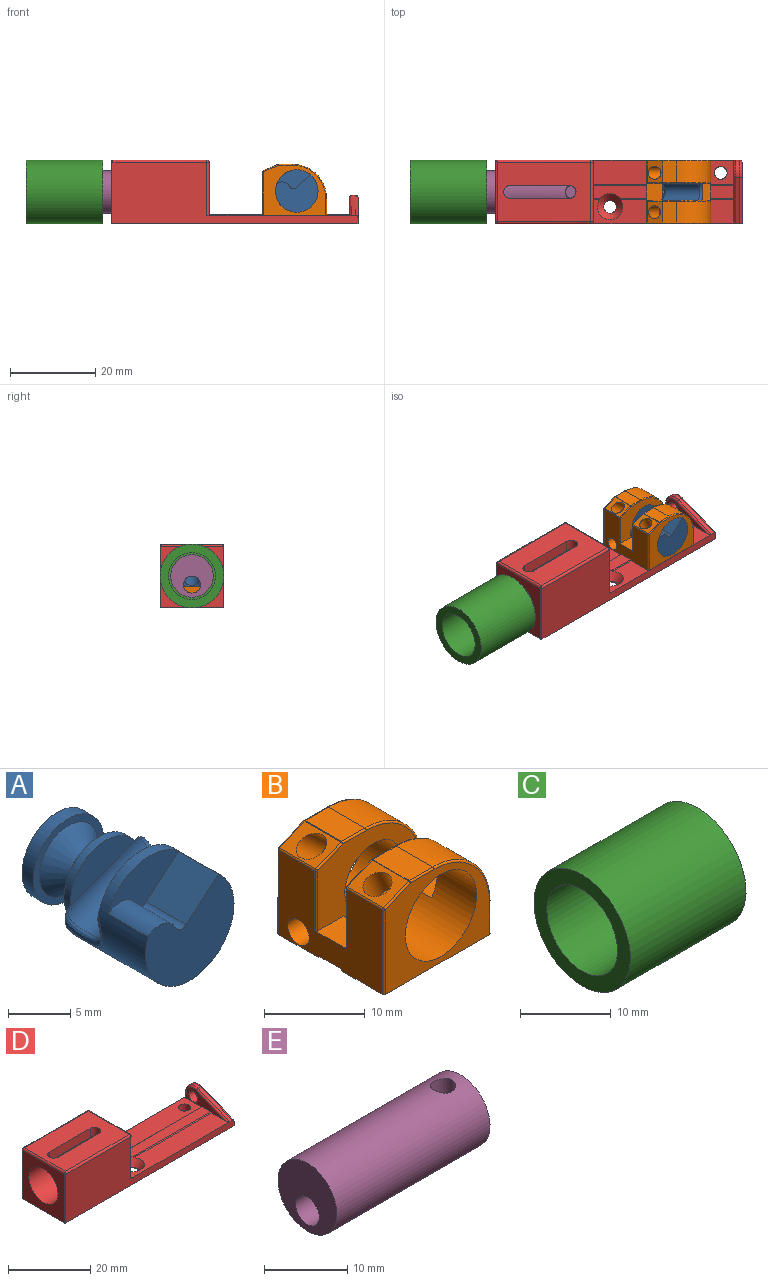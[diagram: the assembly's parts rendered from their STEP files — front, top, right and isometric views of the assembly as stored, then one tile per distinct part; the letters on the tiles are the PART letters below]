
ASSEMBLY  parts=5 mates=5
PART A: 19 faces, bbox 10.2x15.2x10.2 mm
  f0: plane 9.77x7.65mm, normal (0,1,0), area 15.6mm2, adj f1,f3,f15,f17,f18
  f1: cylinder r=5mm len=10mm, axis (0,-1,0), area 180.1mm2, adj f0,f2,f10,f12,f13,f16,f17,f18
  f2: plane 10x8.83mm, normal (0,-1,0), area 59.1mm2, adj f1,f10,f11,f12
  f3: cylinder r=4mm len=8mm, axis (0,1,0), area 18.8mm2, adj f0,f5,f14
  f4: cone r=3.31mm half-angle=45deg, axis (0,-1,0), area 37.8mm2, adj f5,f7
  f5: plane 8x8mm, normal (0,1,0), area 15.9mm2, adj f3,f4
  f6: plane 8x8mm, normal (0,-1,0), area 15.9mm2, adj f7,f9
  f7: cone r=1.56mm half-angle=45deg, axis (0,1,0), area 37.8mm2, adj f4,f6
  f8: plane 8x8mm, normal (0,1,0), area 50.3mm2, adj f9
  f9: cylinder r=4mm len=8mm, axis (0,1,0), area 31.4mm2, adj f6,f8
  f10: cylinder r=2mm len=4.5mm, axis (0,-1,0), area 16.7mm2, adj f1,f2,f11,f13
  f11: cylinder r=0.75mm len=4.5mm, axis (0,-1,0), area 6.3mm2, adj f2,f10,f12,f13
  f12: plane 4.5x3.63mm, normal (-0.65,0,0.76), area 21.6mm2, adj f1,f2,f11,f13
  f13: plane 7.93x4.49mm, normal (0,-1,0), area 19.4mm2, adj f1,f10,f11,f12
  f14: plane 7.26x4.44mm, normal (0,-1,0), area 17.2mm2, adj f3,f15
  f15: cylinder r=2mm len=8.91mm, axis (-0.93,0,-0.36), area 55.1mm2, adj f0,f14,f16,f17,f18
  f16: plane 8.81x5.78mm, normal (0,1,0), area 28.6mm2, adj f1,f15,f17,f18
  f17: bspline ~5x4.19mm, area 6.2mm2, adj f0,f1,f15,f16
  f18: bspline ~5x4.76mm, area 6.2mm2, adj f0,f1,f15,f16
PART B: 56 faces, bbox 16x15.3x13.1 mm
  f0: plane 4.4x2.81mm, normal (0,0,1), area 11.3mm2, adj f5,f16,f18,f19,f38,f54
  f1: cylinder r=8mm len=8mm, axis (0,1,0), area 64.1mm2, adj f2,f5,f25,f37
  f2: plane 5.1x3.28mm, normal (0,0,1), area 16.7mm2, adj f1,f27,f33,f36
  f3: plane 5.1x3.52mm, normal (-0.39,0,0.92), area 12.4mm2, adj f28,f29,f33,f34,f55
  f4: plane 15x5.8mm, normal (0,0,-1), area 87mm2, adj f5,f6,f11,f15,f23,f24
  f5: plane 14.6x4mm, normal (1,0,0), area 46.3mm2, adj f0,f1,f4,f7,f10,f13,f14,f15
  f6: plane 14.6x10.29mm, normal (-1,0,0), area 110.4mm2, adj f4,f10,f13,f14,f15,f17,f22,f24
  f7: cylinder r=8mm len=8mm, axis (0,1,0), area 64.1mm2, adj f5,f8,f42,f53
  f8: plane 5.1x3.28mm, normal (0,0,1), area 16.7mm2, adj f7,f46,f50,f52
  f9: plane 5.39x3.81mm, normal (-0.39,0,0.92), area 11.7mm2, adj f21,f44,f45,f49,f50
  f10: plane 15x5.8mm, normal (0,0,-1), area 87mm2, adj f5,f6,f12,f13,f39,f40
  f11: plane 14.6x11.8mm, normal (0,-1,0), area 78mm2, adj f4,f19,f23,f24,f25,f27,f28
  f12: plane 14.6x11.8mm, normal (0,1,0), area 106.3mm2, adj f10,f20,f39,f40,f42,f45,f46
  f13: plane 15x0.2mm, normal (0,-0.71,-0.71), area 4.2mm2, adj f5,f6,f10,f14
  f14: plane 15x3mm, normal (0,0,-1), area 45mm2, adj f5,f6,f13,f15
  f15: plane 15x0.2mm, normal (0,0.71,-0.71), area 4.2mm2, adj f4,f5,f6,f14
  f16: plane 14.6x8.8mm, normal (0,1,0), area 47.6mm2, adj f0,f17,f19,f30,f34,f36,f37,f38
  f17: plane 4.4x3.81mm, normal (0,0,1), area 15.3mm2, adj f6,f16,f18,f19,f30,f43
  f18: plane 14.6x11.07mm, normal (0,-1,0), area 75.9mm2, adj f0,f17,f19,f20,f43,f49,f52,f53
  f19: cylinder r=5mm len=10mm, axis (0,-1,0), area 200.8mm2, adj f0,f11,f16,f17,f18,f55
  f20: cylinder r=4mm len=8mm, axis (0,1,0), area 112.7mm2, adj f12,f18,f21,f22
  f21: cylinder r=1.5mm len=5.91mm, axis (-0.74,0,0.67), area 41.4mm2, adj f9,f20
  f22: cylinder r=1.5mm len=15mm, axis (1,0,0), area 118.8mm2, adj f5,f6,f20
  f23: cylinder r=0.2mm len=4mm, axis (0,0,-1), area 1.3mm2, adj f4,f5,f11,f25
  f24: cylinder r=0.2mm len=10.29mm, axis (0,0,1), area 3.2mm2, adj f4,f6,f11,f26
  f25: torus R=7.8mm, axis (0,-1,0), area 3.9mm2, adj f1,f11,f23,f27
  f26: sphere r=0.2mm, area 0.1mm2, adj f24,f28,f29
  f27: cylinder r=0.2mm len=3.28mm, axis (1,0,0), area 1mm2, adj f2,f11,f25,f31
  f28: cylinder r=0.2mm len=3.6mm, axis (0.92,0,0.39), area 1.2mm2, adj f3,f11,f26,f31
  f29: cylinder r=0.2mm len=5.1mm, axis (0,-1,0), area 1.2mm2, adj f3,f6,f26,f32
  f30: cylinder r=0.2mm len=7.29mm, axis (0,0,-1), area 2.3mm2, adj f6,f16,f17,f32
  f31: sphere r=0.2mm, area 0mm2, adj f27,f28,f33
  f32: sphere r=0.2mm, area 0mm2, adj f29,f30,f34
  f33: cylinder r=0.2mm len=5.1mm, axis (0,1,0), area 0.4mm2, adj f2,f3,f31,f35
  f34: cylinder r=0.2mm len=3.6mm, axis (-0.92,0,-0.39), area 1.2mm2, adj f3,f16,f32,f35
  f35: sphere r=0.2mm, area 0mm2, adj f33,f34,f36
  f36: cylinder r=0.2mm len=3.28mm, axis (-1,0,0), area 1mm2, adj f2,f16,f35,f37
  f37: torus R=7.8mm, axis (0,-1,0), area 3.9mm2, adj f1,f16,f36,f38
  f38: cylinder r=0.2mm len=1mm, axis (0,0,1), area 0.3mm2, adj f0,f5,f16,f37
  f39: cylinder r=0.2mm len=10.29mm, axis (0,0,-1), area 3.2mm2, adj f6,f10,f12,f41
  f40: cylinder r=0.2mm len=4mm, axis (0,0,1), area 1.3mm2, adj f5,f10,f12,f42
  f41: sphere r=0.2mm, area 0mm2, adj f39,f44,f45
  f42: torus R=7.8mm, axis (0,-1,0), area 3.9mm2, adj f7,f12,f40,f46
  f43: cylinder r=0.2mm len=7.29mm, axis (0,0,1), area 2.3mm2, adj f6,f17,f18,f47
  f44: cylinder r=0.2mm len=5.1mm, axis (0,-1,0), area 1.2mm2, adj f6,f9,f41,f47
  f45: cylinder r=0.2mm len=3.6mm, axis (-0.92,0,-0.39), area 1.2mm2, adj f9,f12,f41,f48
  f46: cylinder r=0.2mm len=3.28mm, axis (-1,0,0), area 1mm2, adj f8,f12,f42,f48
  f47: sphere r=0.2mm, area 0mm2, adj f43,f44,f49
  f48: sphere r=0.2mm, area 0mm2, adj f45,f46,f50
  f49: cylinder r=0.2mm len=3.6mm, axis (0.92,0,0.39), area 1.2mm2, adj f9,f18,f47,f51
  f50: cylinder r=0.2mm len=5.1mm, axis (0,1,0), area 0.4mm2, adj f8,f9,f48,f51
  f51: sphere r=0.2mm, area 0mm2, adj f49,f50,f52
  f52: cylinder r=0.2mm len=3.28mm, axis (1,0,0), area 1mm2, adj f8,f18,f51,f53
  f53: torus R=7.8mm, axis (0,1,0), area 3.9mm2, adj f7,f18,f52,f54
  f54: cylinder r=0.2mm len=1mm, axis (0,0,-1), area 0.3mm2, adj f0,f5,f18,f53
  f55: cylinder r=1.5mm len=8.04mm, axis (-0.39,0,0.92), area 41mm2, adj f3,f19
PART C: 6 faces, bbox 18x15x15 mm
  f0: cylinder r=5mm len=10mm, axis (1,0,0), area 157.1mm2, adj f3,f5
  f1: cylinder r=7.5mm len=18mm, axis (1,0,0), area 848.2mm2, adj f2,f3
  f2: plane 15x15mm, normal (-1,0,0), area 81.7mm2, adj f1,f4
  f3: plane 15x15mm, normal (1,0,0), area 98.2mm2, adj f0,f1
  f4: cylinder r=5.5mm len=13mm, axis (-1,0,0), area 449.2mm2, adj f2,f5
  f5: plane 11x11mm, normal (-1,0,0), area 16.5mm2, adj f0,f4
PART D: 47 faces, bbox 58x15.4x15 mm
  f0: plane 26.6x0.2mm, normal (0,-0.71,0.71), area 7.5mm2, adj f3,f12,f16,f26
  f1: plane 10x10mm, normal (-1,0,0), area 65mm2, adj f17,f18,f25
  f2: plane 1.6x0.2mm, normal (0,-0.71,0.71), area 0.4mm2, adj f3,f11,f12,f26
  f3: plane 33x3mm, normal (0,0,1), area 95mm2, adj f0,f2,f4,f11,f16,f26
  f4: plane 33x0.2mm, normal (0,0.71,0.71), area 9.3mm2, adj f3,f11,f13,f16
  f5: plane 57.3x14.5mm, normal (0,1,0), area 395.1mm2, adj f8,f13,f14,f29,f30,f37,f43,f46
  f6: plane 22x14mm, normal (0,0,1), area 258.9mm2, adj f19,f20,f21,f22,f29,f31,f33,f34
  f7: plane 57.8x14.5mm, normal (0,-1,0), area 394.3mm2, adj f8,f10,f12,f15,f33,f36,f39,f41
  f8: plane 58x15mm, normal (0,0,-1), area 855.8mm2, adj f5,f7,f9,f10,f27,f28,f37,f39
  f9: plane 14.6x14.5mm, normal (-1,0,0), area 133.2mm2, adj f8,f18,f31,f37,f39
  f10: plane 14.5x6.2mm, normal (1,0,0), area 54.2mm2, adj f7,f8,f23,f41,f42,f43
  f11: plane 14x12.5mm, normal (1,0,0), area 154.7mm2, adj f2,f3,f4,f12,f13,f17,f25,f30
  f12: plane 34x5.8mm, normal (0,0,1), area 167.3mm2, adj f0,f2,f7,f11,f16,f26,f36,f44
  f13: plane 34x5.8mm, normal (0,0,1), area 184.4mm2, adj f4,f5,f11,f16,f28,f30,f46
  f14: cylinder r=3mm len=4.14mm, axis (1,0,0), area 5.9mm2, adj f5,f15,f42,f45
  f15: plane 10.86x4.47mm, normal (0,-0.38,0.92), area 11.7mm2, adj f7,f14,f41,f44
  f16: plane 13.19x4.2mm, normal (-1,0,0), area 24.9mm2, adj f0,f3,f4,f12,f13,f23,f44,f45
  f17: cylinder r=2mm len=4mm, axis (1,0,0), area 25.1mm2, adj f1,f11
  f18: cylinder r=5mm len=21mm, axis (1,0,0), area 609.9mm2, adj f1,f9,f19,f20,f21,f22,f24
  f19: cylinder r=1.5mm len=3mm, axis (0,0,1), area 12.3mm2, adj f6,f18,f20,f22
  f20: plane 14x2.73mm, normal (0,1,0), area 38.2mm2, adj f6,f18,f19,f21
  f21: cylinder r=1.5mm len=3mm, axis (0,0,1), area 12.3mm2, adj f6,f18,f20,f22
  f22: plane 14x2.73mm, normal (0,-1,0), area 38.2mm2, adj f6,f18,f19,f21
  f23: cylinder r=1.5mm len=3mm, axis (1,0,0), area 18.8mm2, adj f10,f16
  f24: plane 3x2.99mm, normal (1,0,0), area 6.1mm2, adj f18,f25
  f25: cylinder r=1.5mm len=3mm, axis (1,0,0), area 18.8mm2, adj f1,f11,f24
  f26: cone r=1.5mm half-angle=39.8deg, axis (0,0,1), area 34.6mm2, adj f0,f2,f3,f12,f27
  f27: cylinder r=1.5mm len=3mm, axis (0,0,-1), area 1.9mm2, adj f8,f26
  f28: cylinder r=1.5mm len=3mm, axis (0,0,1), area 18.8mm2, adj f8,f13
  f29: cylinder r=0.5mm len=22.3mm, axis (-1,0,0), area 17.4mm2, adj f5,f6,f32,f38
  f30: cylinder r=0.5mm len=12.5mm, axis (0,0,-1), area 9.8mm2, adj f5,f11,f13,f32
  f31: cylinder r=0.5mm len=14.6mm, axis (0,1,0), area 11.3mm2, adj f6,f9,f38,f40
  f32: sphere r=0.5mm, area 0.4mm2, adj f29,f30,f34
  f33: cylinder r=0.5mm len=22.3mm, axis (1,0,0), area 17.4mm2, adj f6,f7,f35,f40
  f34: cylinder r=0.5mm len=14mm, axis (0,1,0), area 11mm2, adj f6,f11,f32,f35
  f35: sphere r=0.5mm, area 0.4mm2, adj f33,f34,f36
  f36: cylinder r=0.5mm len=12.5mm, axis (0,0,1), area 9.8mm2, adj f7,f11,f12,f35
  f37: cylinder r=0.2mm len=14.5mm, axis (0,0,-1), area 4.6mm2, adj f5,f8,f9,f38
  f38: bspline ~0.59x0.5mm, area 0.2mm2, adj f29,f31,f37
  f39: cylinder r=0.2mm len=14.5mm, axis (0,0,1), area 4.6mm2, adj f7,f8,f9,f40
  f40: bspline ~0.52x0.5mm, area 0.2mm2, adj f31,f33,f39
  f41: cylinder r=0.5mm len=11.24mm, axis (0,-0.92,-0.38), area 9.3mm2, adj f7,f10,f15,f42
  f42: torus R=2.5mm, axis (1,0,0), area 4.3mm2, adj f10,f14,f41,f43
  f43: cylinder r=0.5mm len=3.7mm, axis (0,0,1), area 2.9mm2, adj f5,f8,f10,f42
  f44: cylinder r=0.5mm len=11.05mm, axis (0,0.92,0.38), area 8.9mm2, adj f12,f15,f16,f45
  f45: torus R=2.5mm, axis (1,0,0), area 4.3mm2, adj f14,f16,f44,f46
  f46: cylinder r=0.5mm len=1.7mm, axis (0,0,-1), area 1.3mm2, adj f5,f13,f16,f45
PART E: 8 faces, bbox 26x10x10 mm
  f0: cylinder r=5mm len=26mm, axis (1,0,0), area 809.7mm2, adj f1,f2,f4
  f1: plane 10x10mm, normal (-1,0,0), area 66mm2, adj f0,f3
  f2: plane 10x10mm, normal (1,0,0), area 66mm2, adj f0,f3
  f3: cylinder r=2mm len=26mm, axis (1,0,0), area 311.3mm2, adj f1,f2,f4,f5,f6
  f4: cylinder r=1.5mm len=5.68mm, axis (0,0,1), area 49.1mm2, adj f0,f3
  f5: cylinder r=1.5mm len=3mm, axis (0,0,1), area 1.5mm2, adj f3,f7
  f6: cylinder r=1.5mm len=3mm, axis (0,0,1), area 1.5mm2, adj f3,f7
  f7: plane 3x3mm, normal (0,0,1), area 7.1mm2, adj f5,f6
PLACE A rot(axis=(-0.1,0.99,0.05),0deg) t=(-4.38,0,0)mm
PLACE B t=(-4.38,0,0)mm
PLACE C t=(0.5,0,0)mm
PLACE D at identity fixed
PLACE E t=(0.5,0,0)mm
MATE planar B.f13 <-> D.f4  axis (0,-0.71,-0.71) through (-8.88,1.6,2.1)mm
MATE slider E.f0 <-> D.f18  axis (1,0,0) through (-31,0,7.5)mm
MATE revolute A.f1 <-> B.f19  axis (0,-1,0) through (-8.38,-7.5,7.73)mm
MATE planar B.f4 <-> D.f12  axis (0,0,-1) through (-8.88,-4.6,2)mm
MATE revolute C.f0 <-> D.f18  axis (1,0,0) through (-54,0,7.5)mm
